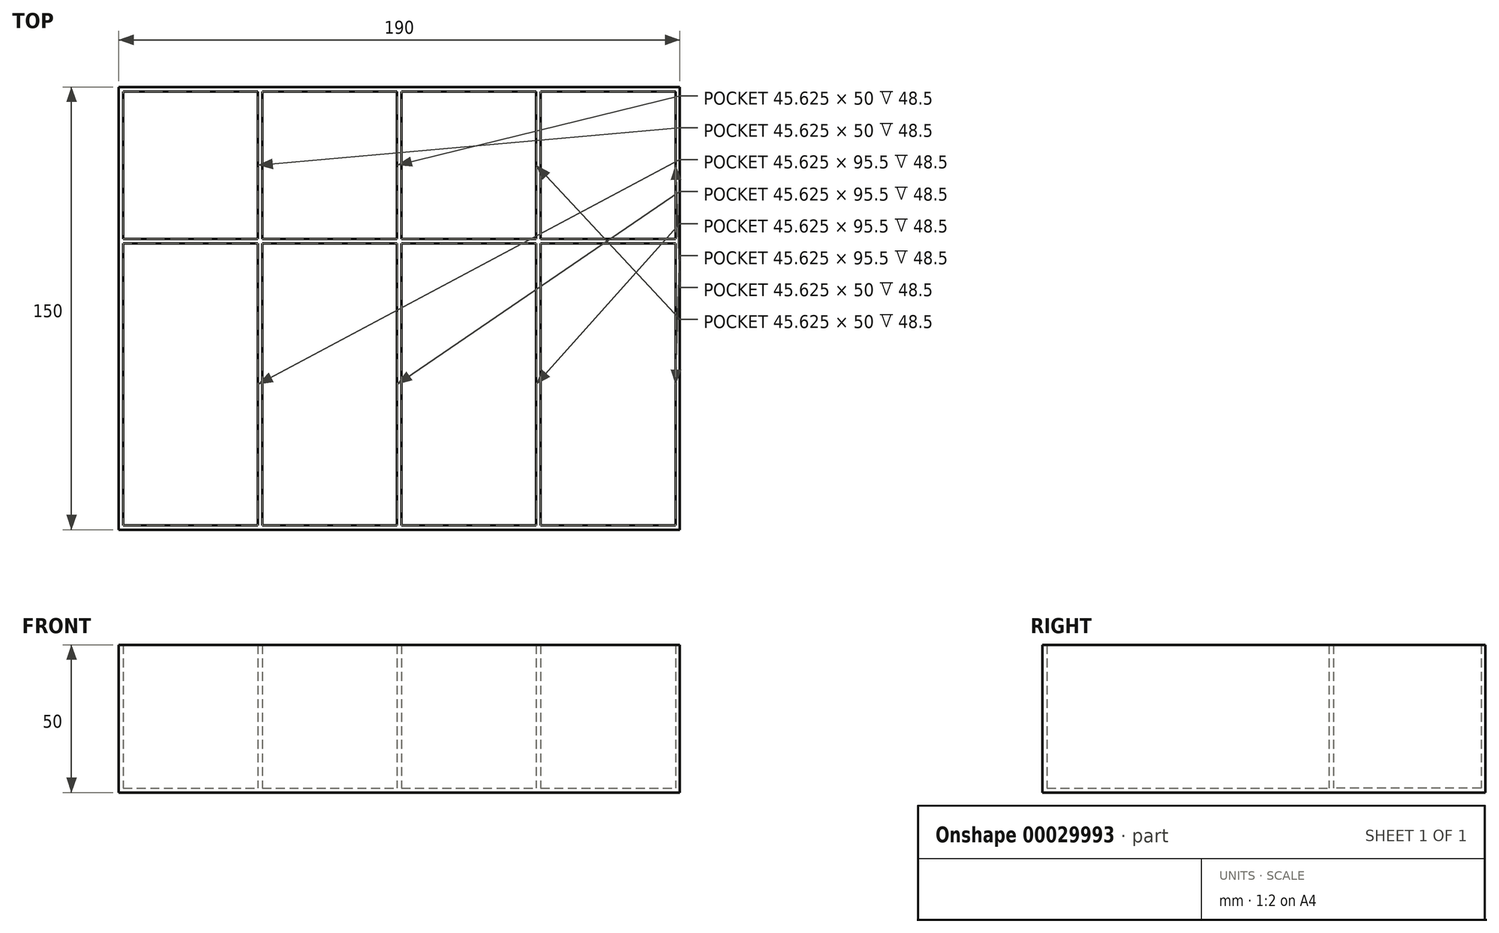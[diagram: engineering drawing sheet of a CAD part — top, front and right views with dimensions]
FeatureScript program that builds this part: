
annotation { "Feature Type Name" : "Feature", "Feature Type Description" : "" }
export const myFeature = defineFeature(function(context is Context, id is Id, definition is map)
    precondition{}
    {
        {
            var Q0;
            Q0=qCreatedBy(makeId("Top.planeOp"),FACE);
            var sketch = newSketch(context, id + "F0", { "sketchPlane" : qUnion([Q0])});
            skLineSegment(sketch, "E0.rect.bottom", {"start": v(-95, 75) * mm, "end": v(95, 75) * mm});
            skLineSegment(sketch, "E0.rect.top", {"start": v(-95, -75) * mm, "end": v(95, -75) * mm});
            skLineSegment(sketch, "E0.rect.left", {"start": v(-95, 75) * mm, "end": v(-95, -75) * mm});
            skLineSegment(sketch, "E0.rect.right", {"start": v(95, 75) * mm, "end": v(95, -75) * mm});
            skPoint(sketch, "E0.rect.middle", {"position": v(0, 0) * mm});
            skSolve(sketch);
        }
        {
            var Q0;
            Q0 = qSketchRegion(id + "F0", true);
            extrude(context, id + "F1", {"entities" : qUnion([Q0]), "depth" : 1.5 * mm});
        }
        {
            var Q0;
            Q0=makeQuery(id+"F1.opExtrude","CAP_FACE",FACE,{"disambiguationData":[OSD([sQuery(id+"F0.wireOp",EDGE,"E0.rect.bottom"),sQuery(id+"F0.wireOp",EDGE,"E0.rect.top"),sQuery(id+"F0.wireOp",EDGE,"E0.rect.left"),sQuery(id+"F0.wireOp",EDGE,"E0.rect.right")])],"isStart":false});
            var sketch = newSketch(context, id + "F2", { "sketchPlane" : qUnion([Q0])});
            skLineSegment(sketch, "E1.bottom", {"start": v(-93.5, 73.5) * mm, "end": v(-47.88, 73.5) * mm});
            skLineSegment(sketch, "E1.top", {"start": v(-93.5, 23.5) * mm, "end": v(-47.88, 23.5) * mm});
            skLineSegment(sketch, "E1.left", {"start": v(-93.5, 73.5) * mm, "end": v(-93.5, 23.5) * mm});
            skLineSegment(sketch, "E1.right", {"start": v(-47.88, 73.5) * mm, "end": v(-47.88, 23.5) * mm});
            skLineSegment(sketch, "E2.1.0.0", {"start": v(-0.75, 73.5) * mm, "end": v(-0.75, 23.5) * mm});
            skLineSegment(sketch, "E2.1.0.1", {"start": v(-46.37, 73.5) * mm, "end": v(-0.75, 73.5) * mm});
            skLineSegment(sketch, "E2.1.0.2", {"start": v(-46.37, 73.5) * mm, "end": v(-46.37, 23.5) * mm});
            skLineSegment(sketch, "E2.1.0.3", {"start": v(-46.37, 23.5) * mm, "end": v(-0.75, 23.5) * mm});
            skLineSegment(sketch, "E2.2.0.0", {"start": v(46.38, 73.5) * mm, "end": v(46.38, 23.5) * mm});
            skLineSegment(sketch, "E2.2.0.1", {"start": v(0.75, 73.5) * mm, "end": v(46.38, 73.5) * mm});
            skLineSegment(sketch, "E2.2.0.2", {"start": v(0.75, 73.5) * mm, "end": v(0.75, 23.5) * mm});
            skLineSegment(sketch, "E2.2.0.3", {"start": v(0.75, 23.5) * mm, "end": v(46.38, 23.5) * mm});
            skLineSegment(sketch, "E2.3.0.0", {"start": v(93.5, 73.5) * mm, "end": v(93.5, 23.5) * mm});
            skLineSegment(sketch, "E2.3.0.1", {"start": v(47.88, 73.5) * mm, "end": v(93.5, 73.5) * mm});
            skLineSegment(sketch, "E2.3.0.2", {"start": v(47.88, 73.5) * mm, "end": v(47.88, 23.5) * mm});
            skLineSegment(sketch, "E2.3.0.3", {"start": v(47.88, 23.5) * mm, "end": v(93.5, 23.5) * mm});
            skLineSegment(sketch, "E2.direction1", {"start": v(-47.88, 23.5) * mm, "end": v(-0.75, 23.5) * mm, "construction": true});
            skLineSegment(sketch, "E3.bottom", {"start": v(-93.5, 22) * mm, "end": v(-47.87, 22) * mm});
            skLineSegment(sketch, "E3.top", {"start": v(-93.5, -73.5) * mm, "end": v(-47.87, -73.5) * mm});
            skLineSegment(sketch, "E3.left", {"start": v(-93.5, 22) * mm, "end": v(-93.5, -73.5) * mm});
            skLineSegment(sketch, "E3.right", {"start": v(-47.87, 22) * mm, "end": v(-47.87, -73.5) * mm});
            skLineSegment(sketch, "E4.bottom", {"start": v(-46.37, 22) * mm, "end": v(-0.75, 22) * mm});
            skLineSegment(sketch, "E4.top", {"start": v(-46.37, -73.5) * mm, "end": v(-0.75, -73.5) * mm});
            skLineSegment(sketch, "E4.left", {"start": v(-46.37, 22) * mm, "end": v(-46.37, -73.5) * mm});
            skLineSegment(sketch, "E4.right", {"start": v(-0.75, 22) * mm, "end": v(-0.75, -73.5) * mm});
            skLineSegment(sketch, "E5.bottom", {"start": v(0.75, 22) * mm, "end": v(46.38, 22) * mm});
            skLineSegment(sketch, "E5.top", {"start": v(0.75, -73.5) * mm, "end": v(46.38, -73.5) * mm});
            skLineSegment(sketch, "E5.left", {"start": v(0.75, 22) * mm, "end": v(0.75, -73.5) * mm});
            skLineSegment(sketch, "E5.right", {"start": v(46.38, 22) * mm, "end": v(46.38, -73.5) * mm});
            skLineSegment(sketch, "E6.bottom", {"start": v(93.5, -73.5) * mm, "end": v(47.88, -73.5) * mm});
            skLineSegment(sketch, "E6.top", {"start": v(93.5, 22) * mm, "end": v(47.88, 22) * mm});
            skLineSegment(sketch, "E6.left", {"start": v(93.5, -73.5) * mm, "end": v(93.5, 22) * mm});
            skLineSegment(sketch, "E6.right", {"start": v(47.88, -73.5) * mm, "end": v(47.88, 22) * mm});
            skSolve(sketch);
        }
        {
            var Q0;
            Q0=makeQuery(id+"F2.imprint","IMPRINT",FACE,{"disambiguationData":[TD([[makeQuery(id+"F2.imprint","IMPRINT",EDGE,{"derivedFrom":sQuery(id+"F2.wireOp",EDGE,"E1.bottom")}),1.0]])]});
            extrude(context, id + "F3", {"entities" : qUnion([Q0]), "operationType" : NewBodyOperationType.ADD, "depth" : (50 - 1.5) * mm});
        }
    });
